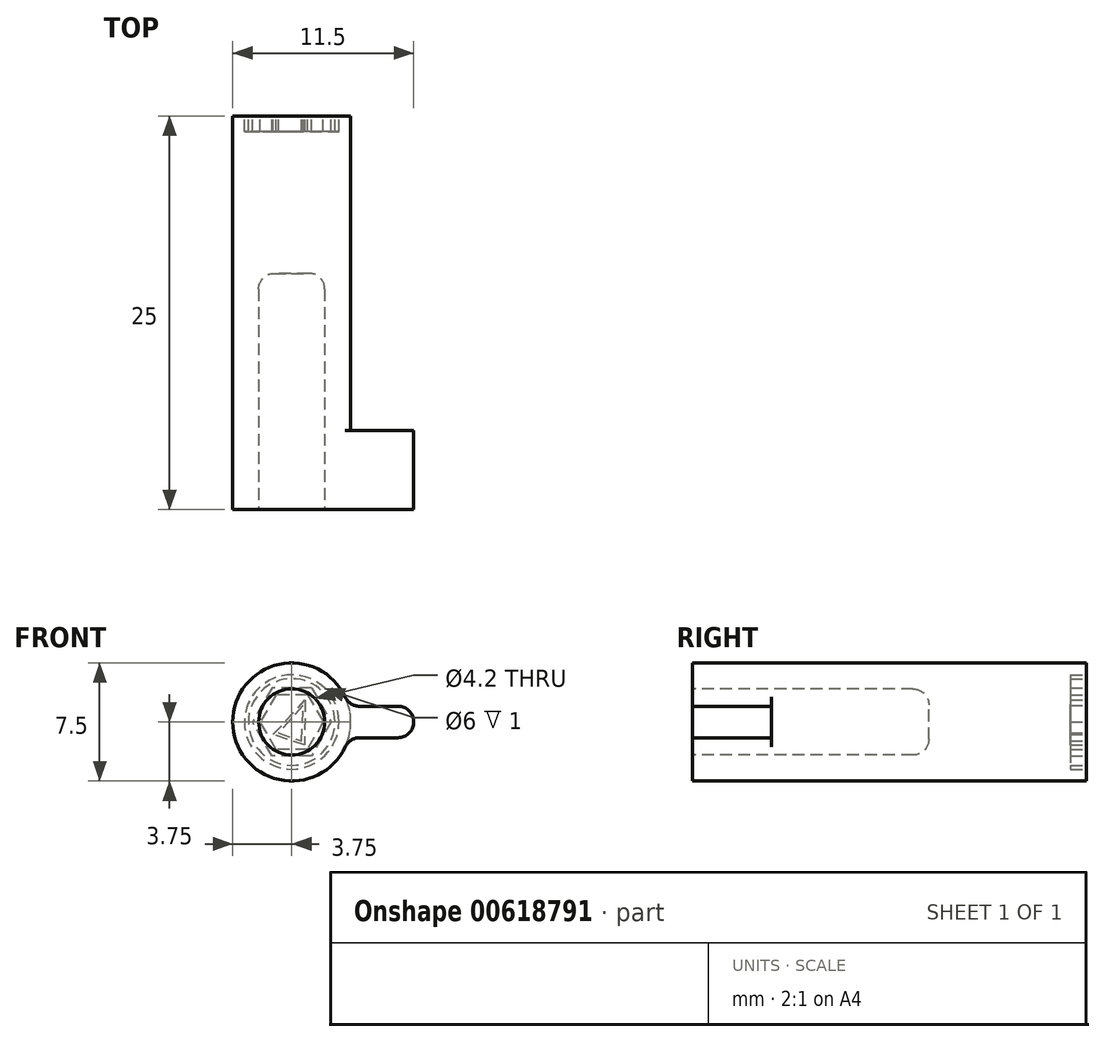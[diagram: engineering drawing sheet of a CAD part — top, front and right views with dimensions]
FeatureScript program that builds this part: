
annotation { "Feature Type Name" : "Feature", "Feature Type Description" : "" }
export const myFeature = defineFeature(function(context is Context, id is Id, definition is map)
    precondition{}
    {
        {
            var Q0;
            Q0=qCreatedBy(makeId("Front.planeOp"),FACE);
            var sketch = newSketch(context, id + "F0", { "sketchPlane" : qUnion([Q0])});
            skCircle(sketch, "E0", {"center": v(0, 0) * mm, "radius": 3.75 * mm});
            skSolve(sketch);
        }
        {
            var Q0;
            Q0 = qSketchRegion(id + "F0", true);
            extrude(context, id + "F1", {"entities" : qUnion([Q0]), "depth" : 25 * mm, "offsetDistance" : 25 * mm});
        }
        {
            var Q0;
            Q0=makeQuery(id+"F1.opExtrude","CAP_FACE",FACE,{"disambiguationData":[OSD([sQuery(id+"F0.wireOp",EDGE,"E0")])],"isStart":false});
            var sketch = newSketch(context, id + "F2", { "sketchPlane" : qUnion([Q0])});
            skLineSegment(sketch, "E1", {"start": v(0, 0) * mm, "end": v(3.75, 0) * mm});
            skLineSegment(sketch, "E2.bottom", {"start": v(7.75, -1) * mm, "end": v(-0.25, -1) * mm});
            skLineSegment(sketch, "E2.top", {"start": v(7.75, 1) * mm, "end": v(-0.25, 1) * mm});
            skLineSegment(sketch, "E2.left", {"start": v(7.75, -1) * mm, "end": v(7.75, 1) * mm});
            skLineSegment(sketch, "E2.right", {"start": v(-0.25, -1) * mm, "end": v(-0.25, 1) * mm});
            skPoint(sketch, "E2.middle", {"position": v(3.75, 0) * mm});
            skSolve(sketch);
        }
        {
            var Q0;
            Q0 = qSketchRegion(id + "F2", true);
            extrude(context, id + "F3", {"entities" : qUnion([Q0]), "operationType" : NewBodyOperationType.ADD, "oppositeDirection" : true, "depth" : 5 * mm, "offsetDistance" : 25 * mm});
        }
        {
            var Q0;
            Q0=makeQuery(id+"F3.boolean.opBoolean","INTERSECT",EDGE,{"derivedFrom":[makeQuery(id+"F1.opExtrude","SWEPT_FACE",FACE,{"disambiguationData":[OSD([sQuery(id+"F0.wireOp",EDGE,"E0")])]}),makeQuery(id+"F3.opExtrude","SWEPT_FACE",FACE,{"disambiguationData":[OSD([sQuery(id+"F2.wireOp",EDGE,"E2.top")])]})]});
            var Q1;
            Q1=makeQuery(id+"F3.boolean.opBoolean","INTERSECT",EDGE,{"derivedFrom":[makeQuery(id+"F1.opExtrude","SWEPT_FACE",FACE,{"disambiguationData":[OSD([sQuery(id+"F0.wireOp",EDGE,"E0")])]}),makeQuery(id+"F3.opExtrude","SWEPT_FACE",FACE,{"disambiguationData":[OSD([sQuery(id+"F2.wireOp",EDGE,"E2.bottom")])]})]});
            var Q2;
            Q2=makeQuery(id+"F3.opExtrude","SWEPT_EDGE",EDGE,{"disambiguationData":[OSD([sQuery(id+"F2.wireOp",EDGE,"E2.top"),sQuery(id+"F2.wireOp",EDGE,"E2.left")])]});
            var Q3;
            Q3=makeQuery(id+"F3.opExtrude","SWEPT_EDGE",EDGE,{"disambiguationData":[OSD([sQuery(id+"F2.wireOp",EDGE,"E2.bottom"),sQuery(id+"F2.wireOp",EDGE,"E2.left")])]});
            fillet(context, id + "F4", {"entities" : qUnion([Q0, Q1, Q2, Q3]), "radius" : 1 * mm, "tangentPropagation" : true, "allowEdgeOverflow" : false});
        }
        {
            var Q0;
            Q0=makeQuery(id+"F3.boolean.opBoolean","MERGE",FACE,{"derivedFrom":[makeQuery(id+"F1.opExtrude","CAP_FACE",FACE,{"disambiguationData":[OSD([sQuery(id+"F0.wireOp",EDGE,"E0")])],"isStart":false}),makeQuery(id+"F3.opExtrude","CAP_FACE",FACE,{"disambiguationData":[OSD([sQuery(id+"F2.wireOp",EDGE,"E2.bottom"),sQuery(id+"F2.wireOp",EDGE,"E2.top"),sQuery(id+"F2.wireOp",EDGE,"E2.left"),sQuery(id+"F2.wireOp",EDGE,"E2.right")])],"isStart":true})]});
            var sketch = newSketch(context, id + "F5", { "sketchPlane" : qUnion([Q0])});
            skCircle(sketch, "E3", {"center": v(0, 0) * mm, "radius": 2.1 * mm});
            skSolve(sketch);
        }
        {
            var Q0;
            Q0 = qSketchRegion(id + "F5", true);
            extrude(context, id + "F6", {"entities" : qUnion([Q0]), "operationType" : NewBodyOperationType.REMOVE, "oppositeDirection" : true, "depth" : 15 * mm, "offsetDistance" : 25 * mm});
        }
        {
            var Q0;
            Q0=makeQuery(id+"F1.opExtrude","CAP_FACE",FACE,{"disambiguationData":[OSD([sQuery(id+"F0.wireOp",EDGE,"E0")])],"isStart":true});
            var sketch = newSketch(context, id + "F7", { "sketchPlane" : qUnion([Q0])});
            skCircle(sketch, "E4", {"center": v(0, 0) * mm, "radius": 2.5 * mm});
            skLineSegment(sketch, "E5", {"start": v(-1.25, 2.17) * mm, "end": v(-2.5, 0) * mm});
            skLineSegment(sketch, "E6", {"start": v(-2.5, 0) * mm, "end": v(-1.25, -2.17) * mm});
            skLineSegment(sketch, "E7", {"start": v(-1.25, -2.17) * mm, "end": v(1.25, -2.17) * mm});
            skLineSegment(sketch, "E8", {"start": v(1.25, -2.17) * mm, "end": v(2.5, 0) * mm});
            skLineSegment(sketch, "E9", {"start": v(-1.25, 2.17) * mm, "end": v(1.25, 2.17) * mm});
            skLineSegment(sketch, "E10", {"start": v(1.25, 2.17) * mm, "end": v(2.5, 0) * mm});
            skCircle(sketch, "E11", {"center": v(0, 0) * mm, "radius": 2 * mm});
            skLineSegment(sketch, "E12", {"start": v(-1, 1.73) * mm, "end": v(-2, 0) * mm});
            skLineSegment(sketch, "E13", {"start": v(-2, 0) * mm, "end": v(-1, -1.73) * mm});
            skLineSegment(sketch, "E14", {"start": v(-1, -1.73) * mm, "end": v(1, -1.73) * mm});
            skLineSegment(sketch, "E15", {"start": v(1, -1.73) * mm, "end": v(2, 0) * mm});
            skLineSegment(sketch, "E16", {"start": v(-1, 1.73) * mm, "end": v(1, 1.73) * mm});
            skLineSegment(sketch, "E17", {"start": v(1, 1.73) * mm, "end": v(2, 0) * mm});
            skCircle(sketch, "E18", {"center": v(0, 0) * mm, "radius": 2.75 * mm});
            skCircle(sketch, "E19", {"center": v(0, 0) * mm, "radius": 3 * mm});
            skLineSegment(sketch, "E20", {"start": v(-1, 1.73) * mm, "end": v(1.5, -0.87) * mm});
            skLineSegment(sketch, "E21", {"start": v(1.5, -0.87) * mm, "end": v(-1, -1.73) * mm});
            skLineSegment(sketch, "E22", {"start": v(-1, 1.73) * mm, "end": v(-1, -1.73) * mm});
            skLineSegment(sketch, "E23", {"start": v(-1, -1.73) * mm, "end": v(-0.62, -1.6) * mm});
            skLineSegment(sketch, "E24", {"start": v(1.5, -0.87) * mm, "end": v(1.12, -1) * mm});
            skLineSegment(sketch, "E25", {"start": v(1.5, -0.87) * mm, "end": v(1.22, -0.58) * mm});
            skLineSegment(sketch, "E26", {"start": v(-1, -1.73) * mm, "end": v(-1, -1.33) * mm});
            skLineSegment(sketch, "E27", {"start": v(-1, 1.73) * mm, "end": v(-1, 1.33) * mm});
            skLineSegment(sketch, "E28", {"start": v(-1, 1.73) * mm, "end": v(-0.72, 1.44) * mm});
            skLineSegment(sketch, "E29", {"start": v(-0.72, 1.44) * mm, "end": v(-1, 1.33) * mm});
            skLineSegment(sketch, "E30", {"start": v(-1, -1.33) * mm, "end": v(-0.62, -1.6) * mm});
            skLineSegment(sketch, "E31", {"start": v(1.22, -0.58) * mm, "end": v(1.12, -1) * mm});
            skLineSegment(sketch, "E32", {"start": v(-0.81, -1.47) * mm, "end": v(1.17, -0.79) * mm});
            skLineSegment(sketch, "E33", {"start": v(1.17, -0.79) * mm, "end": v(-0.86, 1.39) * mm});
            skLineSegment(sketch, "E34", {"start": v(-0.86, 1.39) * mm, "end": v(-0.81, -1.47) * mm});
            skLineSegment(sketch, "E35", {"start": v(-0.81, -1.47) * mm, "end": v(-0.82, -1.07) * mm});
            skLineSegment(sketch, "E36", {"start": v(-0.81, -1.47) * mm, "end": v(-0.43, -1.34) * mm});
            skLineSegment(sketch, "E37", {"start": v(-0.43, -1.34) * mm, "end": v(-0.82, -1.07) * mm});
            skLineSegment(sketch, "E38", {"start": v(1.17, -0.79) * mm, "end": v(0.9, -0.5) * mm});
            skLineSegment(sketch, "E39", {"start": v(1.17, -0.79) * mm, "end": v(0.8, -0.92) * mm});
            skLineSegment(sketch, "E40", {"start": v(0.8, -0.92) * mm, "end": v(0.9, -0.5) * mm});
            skLineSegment(sketch, "E41", {"start": v(-0.86, 1.39) * mm, "end": v(-0.85, 0.99) * mm});
            skLineSegment(sketch, "E42", {"start": v(-0.86, 1.39) * mm, "end": v(-0.59, 1.1) * mm});
            skLineSegment(sketch, "E43", {"start": v(-0.59, 1.1) * mm, "end": v(-0.85, 0.99) * mm});
            skLineSegment(sketch, "E44", {"start": v(-0.72, 1.04) * mm, "end": v(0.85, -0.7) * mm});
            skLineSegment(sketch, "E45", {"start": v(0.85, -0.7) * mm, "end": v(-0.63, -1.2) * mm});
            skLineSegment(sketch, "E46", {"start": v(-0.63, -1.2) * mm, "end": v(-0.72, 1.04) * mm});
            skSolve(sketch);
        }
        {
            var Q0;
            Q0=makeQuery(id+"F7.imprint","IMPRINT",FACE,{"disambiguationData":[TD([[makeQuery(id+"F7.imprint","IMPRINT",EDGE,{"derivedFrom":sQuery(id+"F7.wireOp",EDGE,"E5")}),1.0]])]});
            var Q1;
            {var subQ0=sQuery(id+"F7.wireOp",EDGE,"E12");Q1=makeQuery(id+"F7.imprint","IMPRINT",FACE,{"disambiguationData":[TD([[makeQuery(id+"F7.imprint","IMPRINT",EDGE,{"derivedFrom":subQ0}),-1.0]])]});}
            var Q2;
            {var subQ0=sQuery(id+"F7.wireOp",EDGE,"E16");Q2=makeQuery(id+"F7.imprint","IMPRINT",FACE,{"disambiguationData":[TD([[makeQuery(id+"F7.imprint","IMPRINT",EDGE,{"derivedFrom":subQ0}),1.0]])]});}
            var Q3;
            {var subQ0=sQuery(id+"F7.wireOp",EDGE,"E13");Q3=makeQuery(id+"F7.imprint","IMPRINT",FACE,{"disambiguationData":[TD([[makeQuery(id+"F7.imprint","IMPRINT",EDGE,{"derivedFrom":subQ0}),-1.0]])]});}
            var Q4;
            {var subQ0=sQuery(id+"F7.wireOp",EDGE,"E15");Q4=makeQuery(id+"F7.imprint","IMPRINT",FACE,{"disambiguationData":[TD([[makeQuery(id+"F7.imprint","IMPRINT",EDGE,{"derivedFrom":subQ0}),-1.0]])]});}
            var Q5;
            {var subQ0=sQuery(id+"F7.wireOp",EDGE,"E17");Q5=makeQuery(id+"F7.imprint","IMPRINT",FACE,{"disambiguationData":[TD([[makeQuery(id+"F7.imprint","IMPRINT",EDGE,{"derivedFrom":subQ0}),1.0]])]});}
            var Q6;
            {var subQ0=sQuery(id+"F7.wireOp",EDGE,"E14");Q6=makeQuery(id+"F7.imprint","IMPRINT",FACE,{"disambiguationData":[TD([[makeQuery(id+"F7.imprint","IMPRINT",EDGE,{"derivedFrom":subQ0}),-1.0]])]});}
            var Q7;
            Q7=makeQuery(id+"F7.imprint","IMPRINT",FACE,{"disambiguationData":[TD([[makeQuery(id+"F7.imprint","IMPRINT",EDGE,{"derivedFrom":sQuery(id+"F7.wireOp",EDGE,"E18")}),-1.0]])]});
            var Q8;
            {var subQ0=sQuery(id+"F7.wireOp",EDGE,"E34");Q8=makeQuery(id+"F7.imprint","IMPRINT",FACE,{"disambiguationData":[TD([[makeQuery(id+"F7.imprint","IMPRINT",EDGE,{"derivedFrom":subQ0}),1.0]])]});}
            var Q9;
            {var subQ0=sQuery(id+"F7.wireOp",EDGE,"E41");Q9=makeQuery(id+"F7.imprint","IMPRINT",FACE,{"disambiguationData":[TD([[makeQuery(id+"F7.imprint","IMPRINT",EDGE,{"derivedFrom":subQ0}),1.0]])]});}
            var Q10;
            {var subQ0=sQuery(id+"F7.wireOp",EDGE,"E33");Q10=makeQuery(id+"F7.imprint","IMPRINT",FACE,{"disambiguationData":[TD([[makeQuery(id+"F7.imprint","IMPRINT",EDGE,{"derivedFrom":subQ0}),1.0]])]});}
            var Q11;
            {var subQ0=sQuery(id+"F7.wireOp",EDGE,"E38");Q11=makeQuery(id+"F7.imprint","IMPRINT",FACE,{"disambiguationData":[TD([[makeQuery(id+"F7.imprint","IMPRINT",EDGE,{"derivedFrom":subQ0}),1.0]])]});}
            var Q12;
            {var subQ0=sQuery(id+"F7.wireOp",EDGE,"E32");Q12=makeQuery(id+"F7.imprint","IMPRINT",FACE,{"disambiguationData":[TD([[makeQuery(id+"F7.imprint","IMPRINT",EDGE,{"derivedFrom":subQ0}),1.0]])]});}
            var Q13;
            {var subQ0=sQuery(id+"F7.wireOp",EDGE,"E35");Q13=makeQuery(id+"F7.imprint","IMPRINT",FACE,{"disambiguationData":[TD([[makeQuery(id+"F7.imprint","IMPRINT",EDGE,{"derivedFrom":subQ0}),-1.0]])]});}
            extrude(context, id + "F8", {"entities" : qUnion([Q0, Q1, Q2, Q3, Q4, Q5, Q6, Q7, Q8, Q9, Q10, Q11, Q12, Q13]), "operationType" : NewBodyOperationType.REMOVE, "oppositeDirection" : true, "depth" : 1 * mm, "offsetDistance" : 25 * mm});
        }
        {
            var Q0;
            Q0=makeQuery(id+"F6.boolean.opBoolean","COPY",EDGE,{"derivedFrom":makeQuery(id+"F6.opExtrude","CAP_EDGE",EDGE,{"disambiguationData":[OSD([sQuery(id+"F5.wireOp",EDGE,"E3")])],"isStart":false})});
            fillet(context, id + "F9", {"entities" : qUnion([Q0]), "radius" : 1 * mm, "tangentPropagation" : true, "allowEdgeOverflow" : false});
        }
    });
